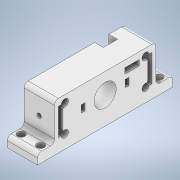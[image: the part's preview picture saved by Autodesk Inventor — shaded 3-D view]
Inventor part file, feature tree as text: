
AUTODESK INVENTOR PART (.ipt)
format: ipt  version: 2020 (Build 240168000, 168)  size: 339,456 bytes
history: native  units: mm
features: extrude x11, sketch x7, other x1, mirror x1, projected_geometry x1
ambient origin geometry x8: Origin, YZ Plane, XZ Plane, XY Plane, X Axis, Y Axis, Z Axis, Center Point
bodies: Body1 (feature_tree)
feature tree (21):
  other  "Bryła1"
  extrude  "Wyciągnięcie proste1"  Depth=33.0mm
  extrude  "Wyciągnięcie proste4"  Depth=10.5mm
  extrude  "Wyciągnięcie proste7"  Depth=40.0mm
  sketch  "Szkic2"
  extrude  "Wyciągnięcie proste5"  Depth=60.0mm
  extrude  "Wyciągnięcie proste6"  Depth=6.0mm
  extrude  "Wyciągnięcie proste9"  Depth=3.5mm
  extrude  "Wyciągnięcie proste10"  TaperAngle=150.0deg  [1 undecoded]
  mirror  "Odbij3"
  extrude  "Wyciągnięcie proste11"  TaperAngle=150.0deg  [1 undecoded]
  extrude  "Wyciągnięcie proste12"  Depth=26.0mm
  sketch  "Szkic7"
  extrude  "Wyciągnięcie proste13"  Depth=13.0mm
  extrude  "Wyciągnięcie proste14"  Depth=6.0mm
  sketch  "Szkic3"
  projected_geometry  "Pętla rzutowana1"
  sketch  "Szkic4"
  sketch  "Szkic5"
  sketch  "Szkic6"
  sketch  "Szkic10"
note: 2 required parameter values undecoded (feature->parameter linkage not recoverable at this tier; creation-order binding heuristic only, values carry confidence <= 0.55)
